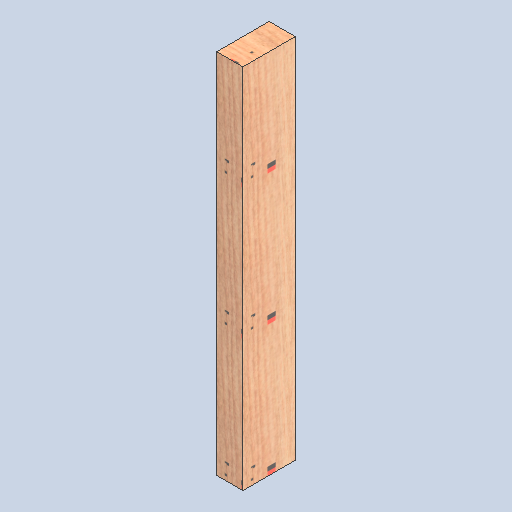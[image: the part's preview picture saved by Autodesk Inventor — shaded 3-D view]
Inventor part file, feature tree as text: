
AUTODESK INVENTOR PART (.ipt)
format: ipt  version: 2025 (Build 290162000, 162)  size: 349,184 bytes
history: native  units: in
note: dims shown in document units (in); Inventor stores cm internally (conversion verified against a paired STEP export)
features: extrude x1, sketch x1
ambient origin geometry x8: Origin, YZ Plane, XZ Plane, XY Plane, X Axis, Y Axis, Z Axis, Center Point
bodies: Solid1 (feature_tree)
feature tree (2):
  extrude  "Extrusion1"  Depth=4.0in
  sketch  "Sketch1"  dims[d0=2.0in d1=4.0in d2=28.0in d3=0.0in]
